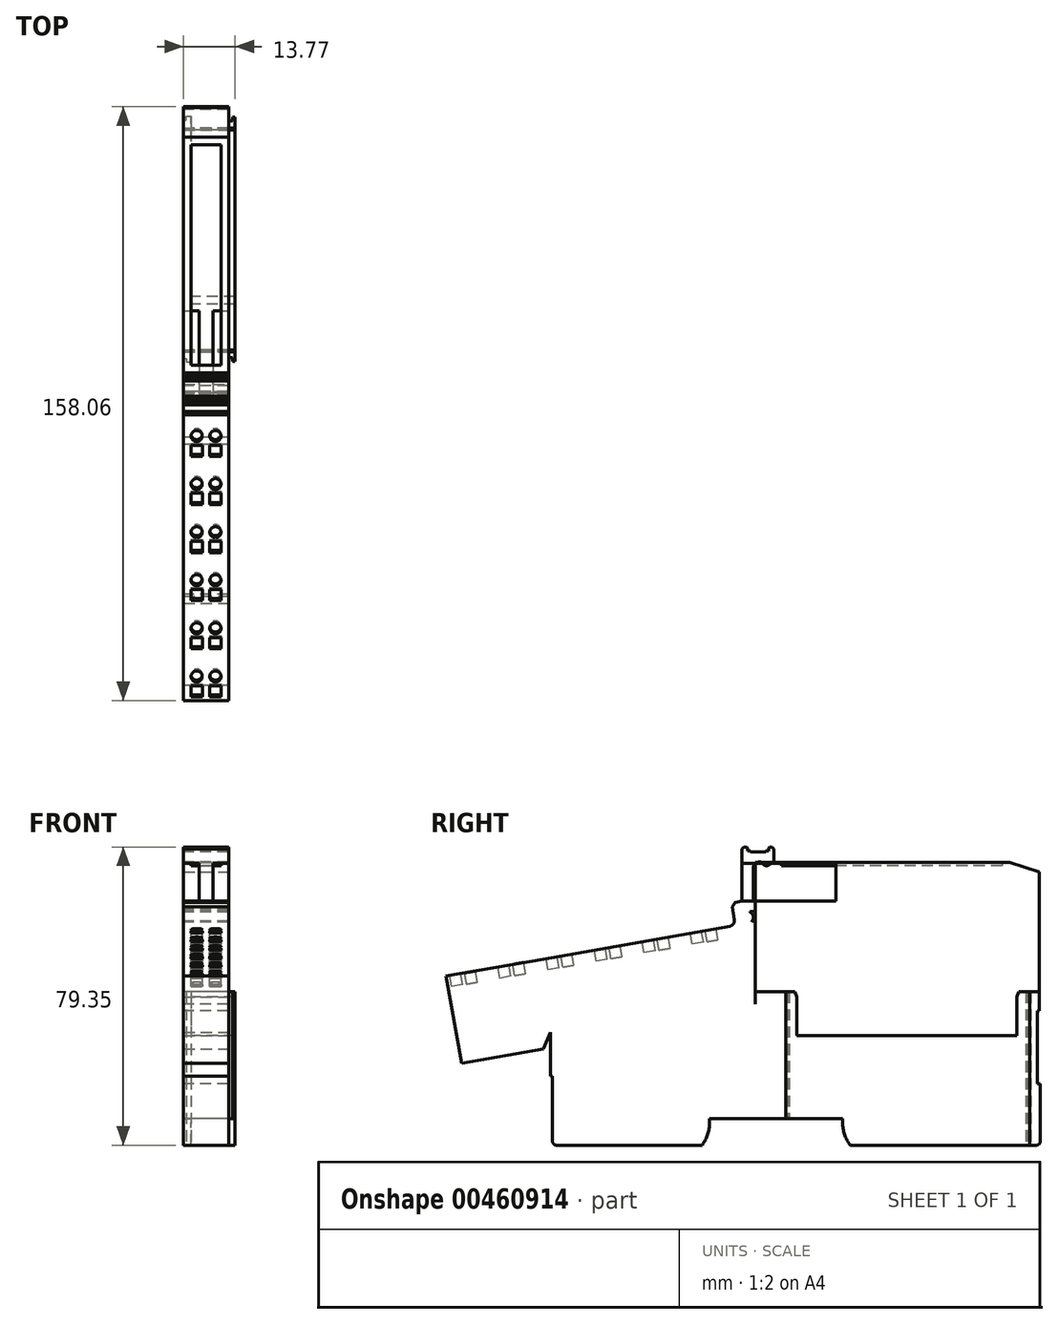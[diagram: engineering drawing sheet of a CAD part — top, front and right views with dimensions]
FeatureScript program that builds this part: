
annotation { "Feature Type Name" : "Feature", "Feature Type Description" : "" }
export const myFeature = defineFeature(function(context is Context, id is Id, definition is map)
    precondition{}
    {
        {
            var Q0;
            Q0=qCreatedBy(makeId("Right.planeOp"),FACE);
            var sketch = newSketch(context, id + "F0", { "sketchPlane" : qUnion([Q0])});
            skLineSegment(sketch, "E0", {"start": v(-59.26, 11.1) * mm, "end": v(-59.26, 24.1) * mm});
            skLineSegment(sketch, "E1", {"start": v(-58.76, -6.2) * mm, "end": v(-58.76, 11.1) * mm});
            skLineSegment(sketch, "E2", {"start": v(-57.26, 21.1) * mm, "end": v(-57.26, 21.9) * mm});
            skLineSegment(sketch, "E3", {"start": v(-57, 22.32) * mm, "end": v(-57, 22.69) * mm});
            skLineSegment(sketch, "E4", {"start": v(-62.03, 41.17) * mm, "end": v(-58.92, 23.54) * mm});
            skLineSegment(sketch, "E5", {"start": v(-8.32, 71.64) * mm, "end": v(-7.82, 72.14) * mm});
            skLineSegment(sketch, "E6", {"start": v(-57.76, -7.2) * mm, "end": v(-18.96, -7.2) * mm});
            skLineSegment(sketch, "E7", {"start": v(20.44, -7.2) * mm, "end": v(70, -7.2) * mm});
            skLineSegment(sketch, "E8", {"start": v(-1.27, 71.9) * mm, "end": v(-1.02, 72.14) * mm});
            skLineSegment(sketch, "E9", {"start": v(0.18, 68.14) * mm, "end": v(-1.32, 67.28) * mm});
            skLineSegment(sketch, "E10", {"start": v(-16.96, -0.2) * mm, "end": v(18.44, -0.2) * mm});
            skLineSegment(sketch, "E11", {"start": v(-10.97, 56.26) * mm, "end": v(-10.16, 57.42) * mm});
            skLineSegment(sketch, "E12", {"start": v(-16.96, -1.2) * mm, "end": v(-16.96, -0.2) * mm});
            skLineSegment(sketch, "E13", {"start": v(-4.8, 55.42) * mm, "end": v(-5.01, 55.13) * mm});
            skLineSegment(sketch, "E14", {"start": v(70.24, 9.16) * mm, "end": v(71, 9.16) * mm});
            skLineSegment(sketch, "E15", {"start": v(-59.26, 11.1) * mm, "end": v(-58.76, 11.1) * mm});
            skLineSegment(sketch, "E16", {"start": v(-8.32, 57.75) * mm, "end": v(-8.32, 71.64) * mm});
            skLineSegment(sketch, "E17", {"start": v(-6.87, 71.14) * mm, "end": v(-6.87, 71.9) * mm});
            skLineSegment(sketch, "E18", {"start": v(-5.32, 57.86) * mm, "end": v(-5.32, 66.64) * mm});
            skLineSegment(sketch, "E19", {"start": v(6.24, 21.9) * mm, "end": v(64.74, 21.9) * mm});
            skLineSegment(sketch, "E20", {"start": v(-10.97, 56.26) * mm, "end": v(-10.37, 52.82) * mm});
            skLineSegment(sketch, "E21", {"start": v(-4.8, 57.5) * mm, "end": v(-4.8, 55.42) * mm});
            skLineSegment(sketch, "E22", {"start": v(-4.8, 52.17) * mm, "end": v(-4.8, 30.34) * mm});
            skLineSegment(sketch, "E23", {"start": v(-4.76, 30.35) * mm, "end": v(-4.76, 33.6) * mm});
            skLineSegment(sketch, "E24", {"start": v(-1.27, 71.9) * mm, "end": v(-1.27, 71.14) * mm});
            skLineSegment(sketch, "E25", {"start": v(-59.26, 24.1) * mm, "end": v(-59.02, 24.1) * mm});
            skLineSegment(sketch, "E26", {"start": v(0.18, 68.14) * mm, "end": v(0.18, 71.64) * mm});
            skLineSegment(sketch, "E27", {"start": v(-57.26, 21.1) * mm, "end": v(-4.76, 30.35) * mm});
            skLineSegment(sketch, "E28", {"start": v(70.24, 28.6) * mm, "end": v(70.74, 28.6) * mm});
            skLineSegment(sketch, "E29", {"start": v(6.24, 21.9) * mm, "end": v(6.24, 32.22) * mm});
            skLineSegment(sketch, "E30", {"start": v(-58.92, 23.54) * mm, "end": v(-58.18, 23.67) * mm});
            skLineSegment(sketch, "E31", {"start": v(-4.76, 33.6) * mm, "end": v(5.74, 33.6) * mm});
            skLineSegment(sketch, "E32", {"start": v(65.24, 33.6) * mm, "end": v(70.74, 33.6) * mm});
            skLineSegment(sketch, "E33", {"start": v(5.74, 33.6) * mm, "end": v(6.24, 32.22) * mm});
            skLineSegment(sketch, "E34", {"start": v(-5.1, 52.38) * mm, "end": v(-4.8, 52.17) * mm});
            skLineSegment(sketch, "E35", {"start": v(18.44, -1.2) * mm, "end": v(18.44, -0.2) * mm});
            skLineSegment(sketch, "E36", {"start": v(-5.32, 57.86) * mm, "end": v(-4.8, 57.5) * mm});
            skLineSegment(sketch, "E37", {"start": v(-11.58, 51.08) * mm, "end": v(-61.22, 42.33) * mm});
            skLineSegment(sketch, "E38", {"start": v(-5.1, 52.38) * mm, "end": v(-5.74, 52.26) * mm});
            skLineSegment(sketch, "E39", {"start": v(-2.53, 67.44) * mm, "end": v(-3.24, 68.14) * mm});
            skLineSegment(sketch, "E40", {"start": v(-7.12, 72.14) * mm, "end": v(-6.87, 71.9) * mm});
            skLineSegment(sketch, "E41", {"start": v(-6.21, 54.92) * mm, "end": v(-5.01, 55.13) * mm});
            skLineSegment(sketch, "E42", {"start": v(-0.32, 72.14) * mm, "end": v(0.18, 71.64) * mm});
            skLineSegment(sketch, "E43", {"start": v(-8.32, 57.75) * mm, "end": v(-10.16, 57.42) * mm});
            skLineSegment(sketch, "E44", {"start": v(-3.82, 68.14) * mm, "end": v(-3.24, 68.14) * mm});
            skLineSegment(sketch, "E45", {"start": v(-6.07, 70.9) * mm, "end": v(-2.07, 70.9) * mm});
            skLineSegment(sketch, "E46", {"start": v(-1.27, 71.14) * mm, "end": v(-1.82, 71.14) * mm});
            skLineSegment(sketch, "E47", {"start": v(-6.32, 71.14) * mm, "end": v(-6.87, 71.14) * mm});
            skLineSegment(sketch, "E48", {"start": v(-0.32, 72.14) * mm, "end": v(-1.02, 72.14) * mm});
            skLineSegment(sketch, "E49", {"start": v(-7.12, 72.14) * mm, "end": v(-7.82, 72.14) * mm});
            skLineSegment(sketch, "E50", {"start": v(64.74, 32.22) * mm, "end": v(65.24, 33.6) * mm});
            skLineSegment(sketch, "E51", {"start": v(64.74, 21.9) * mm, "end": v(64.74, 32.22) * mm});
            skLineSegment(sketch, "E52", {"start": v(70.24, 9.16) * mm, "end": v(70.24, 28.6) * mm});
            skLineSegment(sketch, "E53", {"start": v(70.74, 28.6) * mm, "end": v(70.74, 33.6) * mm});
            skLineSegment(sketch, "E54", {"start": v(71, 9.16) * mm, "end": v(71, -6.2) * mm});
            skArc(sketch, "E55", {"start": v(-18.96, -7.2) * mm, "mid": v(-17.47, -4.37) * mm, "end": v(-16.96, -1.2) * mm});
            skArc(sketch, "E56", {"start": v(18.44, -1.2) * mm, "mid": v(18.95, -4.37) * mm, "end": v(20.44, -7.2) * mm});
            skArc(sketch, "E57", {"start": v(-6.21, 54.81) * mm, "mid": v(-5.35, 53.73) * mm, "end": v(-5.74, 52.4) * mm});
            skArc(sketch, "E58", {"start": v(-3.82, 68.14) * mm, "mid": v(-4.88, 67.7) * mm, "end": v(-5.32, 66.64) * mm});
            skArc(sketch, "E59", {"start": v(-11.58, 51.08) * mm, "mid": v(-10.62, 51.7) * mm, "end": v(-10.37, 52.82) * mm});
            skArc(sketch, "E60", {"start": v(-57.26, 21.9) * mm, "mid": v(-57.1, 22.1) * mm, "end": v(-57, 22.32) * mm});
            skArc(sketch, "E61", {"start": v(-2.53, 67.44) * mm, "mid": v(-1.95, 67.15) * mm, "end": v(-1.32, 67.28) * mm});
            skArc(sketch, "E62", {"start": v(-61.22, 42.33) * mm, "mid": v(-61.86, 41.92) * mm, "end": v(-62.03, 41.17) * mm});
            skArc(sketch, "E63", {"start": v(-57, 22.69) * mm, "mid": v(-57.37, 23.45) * mm, "end": v(-58.18, 23.67) * mm});
            skArc(sketch, "E64", {"start": v(-58.76, -6.2) * mm, "mid": v(-58.47, -6.91) * mm, "end": v(-57.76, -7.2) * mm});
            skArc(sketch, "E65", {"start": v(70, -7.2) * mm, "mid": v(70.7, -6.91) * mm, "end": v(71, -6.2) * mm});
            skArc(sketch, "E66", {"start": v(-6.07, 70.9) * mm, "mid": v(-6.15, 71.07) * mm, "end": v(-6.32, 71.14) * mm});
            skArc(sketch, "E67", {"start": v(-1.82, 71.14) * mm, "mid": v(-2, 71.07) * mm, "end": v(-2.07, 70.9) * mm});
            skLineSegment(sketch, "E68", {"start": v(-6.21, 54.92) * mm, "end": v(-6.21, 54.81) * mm});
            skLineSegment(sketch, "E69", {"start": v(-5.74, 52.26) * mm, "end": v(-5.74, 52.4) * mm});
            skSolve(sketch);
        }
        {
            var Q0;
            Q0=makeQuery(id+"F0.imprint","IMPRINT",FACE,{"disambiguationData":[TD([[makeQuery(id+"F0.imprint","IMPRINT",EDGE,{"derivedFrom":sQuery(id+"F0.wireOp",EDGE,"E0")}),-1.0]])]});
            extrude(context, id + "F1", {"entities" : qUnion([Q0]), "depth" : 25 * mm, "offsetDistance" : 25 * mm, "symmetric" : true});
        }
        {
            var Q0;
            {var subQ2=sQuery(id+"F0.wireOp",EDGE,"E2");Q0=makeQuery(id+"F0.imprint","IMPRINT",FACE,{"disambiguationData":[TD([[makeQuery(id+"F0.imprint","IMPRINT",EDGE,{"derivedFrom":subQ2}),-1.0]])]});}
            extrude(context, id + "F2", {"entities" : qUnion([Q0]), "depth" : 25 * mm, "offsetDistance" : 25 * mm, "symmetric" : true});
        }
        {
            var Q0;
            Q0=makeQuery(id+"F1.opExtrude","SWEPT_FACE",FACE,{"disambiguationData":[OSD([sQuery(id+"F0.wireOp",EDGE,"E7")])]});
            var sketch = newSketch(context, id + "F3", { "sketchPlane" : qUnion([Q0])});
            skLineSegment(sketch, "E70.MirrorCS", {"start": v(4.65, -4.25) * mm, "end": v(5.65, -4.25) * mm});
            skLineSegment(sketch, "E71.MirrorCS", {"start": v(5.65, -4.25) * mm, "end": v(5.65, -3.25) * mm});
            skLineSegment(sketch, "E72.MirrorCS", {"start": v(5.65, -3.25) * mm, "end": v(6.4, -3.25) * mm});
            skLineSegment(sketch, "E73.MirrorCS", {"start": v(-6.6, -67.5) * mm, "end": v(-6.6, -68.5) * mm});
            skLineSegment(sketch, "E74.MirrorCS", {"start": v(-6.6, -68.5) * mm, "end": v(-5.35, -68.5) * mm});
            skLineSegment(sketch, "E75.MirrorCS", {"start": v(-6.6, -4) * mm, "end": v(-7.35, -4) * mm});
            skLineSegment(sketch, "E76.MirrorCS", {"start": v(-7.37, -67.5) * mm, "end": v(-7.37, -72.33) * mm});
            skLineSegment(sketch, "E77.MirrorCS", {"start": v(-7.37, -67.5) * mm, "end": v(-6.6, -67.5) * mm});
            skLineSegment(sketch, "E78.MirrorCS", {"start": v(-6.6, -3) * mm, "end": v(-6.6, -4) * mm});
            skLineSegment(sketch, "E79.MirrorCS", {"start": v(-5.35, -3) * mm, "end": v(-6.6, -3) * mm});
            skLineSegment(sketch, "E80.MirrorCS", {"start": v(5.65, -67.25) * mm, "end": v(4.65, -67.25) * mm});
            skLineSegment(sketch, "E81.MirrorCS", {"start": v(4.65, -67.25) * mm, "end": v(4.65, -72.33) * mm});
            skLineSegment(sketch, "E82.MirrorCS", {"start": v(5.65, -68.25) * mm, "end": v(5.65, -67.25) * mm});
            skLineSegment(sketch, "E83.MirrorCS", {"start": v(6.4, -68.25) * mm, "end": v(5.65, -68.25) * mm});
            skLineSegment(sketch, "E84.MirrorCS", {"start": v(-5.35, -3) * mm, "end": v(-5.35, -68.5) * mm});
            skLineSegment(sketch, "E85.MirrorCS", {"start": v(6.4, -3.25) * mm, "end": v(6.4, -68.25) * mm});
            skLineSegment(sketch, "E86.MirrorCS", {"start": v(-7.35, -4) * mm, "end": v(-7.35, 62.03) * mm});
            skLineSegment(sketch, "E87.MirrorCS", {"start": v(4.65, 62.03) * mm, "end": v(-7.35, 62.03) * mm});
            skLineSegment(sketch, "E88.MirrorCS", {"start": v(-7.37, -72.33) * mm, "end": v(4.65, -72.33) * mm});
            skLineSegment(sketch, "E89.MirrorCS", {"start": v(4.65, 62.03) * mm, "end": v(4.65, -4.25) * mm});
            skLineSegment(sketch, "E90.bottom", {"start": v(43.3, -96.21) * mm, "end": v(-50.8, -96.21) * mm});
            skLineSegment(sketch, "E90.top", {"start": v(43.3, 101.45) * mm, "end": v(-50.8, 101.45) * mm});
            skLineSegment(sketch, "E90.left", {"start": v(43.3, -96.21) * mm, "end": v(43.3, 101.45) * mm});
            skLineSegment(sketch, "E90.right", {"start": v(-50.8, -96.21) * mm, "end": v(-50.8, 101.45) * mm});
            skSolve(sketch);
        }
        {
            var Q0;
            Q0=makeQuery(id+"F3.imprint","IMPRINT",FACE,{"disambiguationData":[TD([[makeQuery(id+"F3.imprint","IMPRINT",EDGE,{"derivedFrom":sQuery(id+"F3.wireOp",EDGE,"E70.MirrorCS")}),1.0]])]});
            var Q1;
            {var subQ2=sQuery(id+"F3.wireOp",EDGE,"E80.MirrorCS");Q1=makeQuery(id+"F3.imprint","IMPRINT",FACE,{"disambiguationData":[TD([[makeQuery(id+"F3.imprint","IMPRINT",EDGE,{"derivedFrom":subQ2}),1.0]])]});}
            var Q2;
            Q2=makeQuery(id+"F3.imprint","IMPRINT",FACE,{"disambiguationData":[TD([[makeQuery(id+"F3.imprint","IMPRINT",EDGE,{"derivedFrom":sQuery(id+"F3.wireOp",EDGE,"E73.MirrorCS")}),1.0]])]});
            extrude(context, id + "F4", {"entities" : qUnion([Q0, Q1, Q2]), "operationType" : NewBodyOperationType.REMOVE, "endBound" : BoundingType.THROUGH_ALL, "oppositeDirection" : true, "depth" : 25 * mm, "offsetDistance" : 25 * mm});
        }
        {
            var Q0;
            Q0=makeQuery(id+"F4.boolean.opBoolean","COPY",FACE,{"derivedFrom":makeQuery(id+"F4.opExtrude","SWEPT_FACE",FACE,{"disambiguationData":[OSD([sQuery(id+"F3.wireOp",EDGE,"E85.MirrorCS")])]})});
            var sketch = newSketch(context, id + "F5", { "sketchPlane" : qUnion([Q0])});
            skLineSegment(sketch, "E91.0", {"start": v(64.74, 21.9) * mm, "end": v(6.24, 21.9) * mm});
            skLineSegment(sketch, "E92.0", {"start": v(6.24, 32.22) * mm, "end": v(6.24, 21.9) * mm});
            skLineSegment(sketch, "E93.0", {"start": v(6.24, 32.22) * mm, "end": v(5.74, 33.6) * mm});
            skLineSegment(sketch, "E94.0", {"start": v(5.74, 33.6) * mm, "end": v(4.25, 33.6) * mm});
            skLineSegment(sketch, "E95.0", {"start": v(3.25, 33.6) * mm, "end": v(-4.76, 33.6) * mm});
            skPoint(sketch, "E96.orphan", {"position": v(3.25, 33.6) * mm});
            skLineSegment(sketch, "E97", {"start": v(3.25, 33.6) * mm, "end": v(4.25, 33.6) * mm});
            skLineSegment(sketch, "E98.0", {"start": v(64.74, 32.22) * mm, "end": v(64.74, 21.9) * mm});
            skLineSegment(sketch, "E98.1", {"start": v(65.24, 33.6) * mm, "end": v(64.74, 32.22) * mm});
            skLineSegment(sketch, "E98.2", {"start": v(67.25, 33.6) * mm, "end": v(65.24, 33.6) * mm});
            skLineSegment(sketch, "E98.3", {"start": v(70.74, 33.6) * mm, "end": v(68.25, 33.6) * mm});
            skPoint(sketch, "E99.orphan", {"position": v(67.25, 33.6) * mm});
            skLineSegment(sketch, "E100", {"start": v(67.25, 33.6) * mm, "end": v(68.25, 33.6) * mm});
            skLineSegment(sketch, "E101", {"start": v(-4.76, 33.6) * mm, "end": v(-4.76, 68.1) * mm});
            skLineSegment(sketch, "E102", {"start": v(-4.76, 68.1) * mm, "end": v(62.88, 68.1) * mm});
            skLineSegment(sketch, "E103", {"start": v(62.88, 68.1) * mm, "end": v(70.74, 65.5) * mm});
            skLineSegment(sketch, "E104", {"start": v(70.74, 65.5) * mm, "end": v(70.74, 33.6) * mm});
            skSolve(sketch);
        }
        {
            var Q0;
            Q0=makeQuery(id+"F5.imprint","IMPRINT",FACE,{"disambiguationData":[TD([[makeQuery(id+"F5.imprint","IMPRINT",EDGE,{"derivedFrom":sQuery(id+"F5.wireOp",EDGE,"E91.0")}),-1.0]])]});
            extrude(context, id + "F6", {"entities" : qUnion([Q0]), "oppositeDirection" : true, "depth" : 12 * mm, "offsetDistance" : 25 * mm});
        }
        {
            var Q0;
            Q0=makeQuery(id+"F6.opExtrude","SWEPT_BODY",BODY,{"disambiguationData":[OSD([sQuery(id+"F5.wireOp",EDGE,"E91.0"),sQuery(id+"F5.wireOp",EDGE,"E92.0"),sQuery(id+"F5.wireOp",EDGE,"E93.0"),sQuery(id+"F5.wireOp",EDGE,"E94.0"),sQuery(id+"F5.wireOp",EDGE,"E95.0"),sQuery(id+"F5.wireOp",EDGE,"E97"),sQuery(id+"F5.wireOp",EDGE,"E98.0"),sQuery(id+"F5.wireOp",EDGE,"E98.1"),sQuery(id+"F5.wireOp",EDGE,"E98.2"),sQuery(id+"F5.wireOp",EDGE,"E98.3"),sQuery(id+"F5.wireOp",EDGE,"E100"),sQuery(id+"F5.wireOp",EDGE,"E101"),sQuery(id+"F5.wireOp",EDGE,"E102"),sQuery(id+"F5.wireOp",EDGE,"E103"),sQuery(id+"F5.wireOp",EDGE,"E104")])]});
            var Q1;
            Q1=makeQuery(id+"F2.opExtrude","SWEPT_EDGE",EDGE,{"disambiguationData":[OSD([sQuery(id+"F0.wireOp",EDGE,"E16"),sQuery(id+"F0.wireOp",EDGE,"E43")])]});
            var Q2;
            Q2=makeQuery(id+"F2.opExtrude","SWEPT_EDGE",EDGE,{"disambiguationData":[OSD([sQuery(id+"F0.wireOp",EDGE,"E11"),sQuery(id+"F0.wireOp",EDGE,"E20")])]});
            transform(context, id + "F7", {"entities" : qUnion([Q0]), "transformType" : TransformType.TRANSLATION_DISTANCE, "transformDirection" : qUnion([Q2]), "distance" : 1.75 * mm, "makeCopy" : false});
        }
        {
            var Q0;
            Q0=makeQuery(id+"F2.opExtrude","SWEPT_FACE",FACE,{"disambiguationData":[OSD([sQuery(id+"F0.wireOp",EDGE,"E16")])]});
            var sketch = newSketch(context, id + "F8", { "sketchPlane" : qUnion([Q0])});
            skLineSegment(sketch, "E105.bottom", {"start": v(-7.35, 67.79) * mm, "end": v(-3.24, 67.79) * mm});
            skLineSegment(sketch, "E105.top", {"start": v(-7.35, 57.75) * mm, "end": v(-3.24, 57.75) * mm});
            skLineSegment(sketch, "E105.left", {"start": v(-7.35, 67.79) * mm, "end": v(-7.35, 57.75) * mm});
            skLineSegment(sketch, "E105.right", {"start": v(-3.24, 67.79) * mm, "end": v(-3.24, 57.75) * mm});
            skLineSegment(sketch, "E106.bottom", {"start": v(0.54, 67.79) * mm, "end": v(4.65, 67.79) * mm});
            skLineSegment(sketch, "E106.top", {"start": v(0.54, 57.75) * mm, "end": v(4.65, 57.75) * mm});
            skLineSegment(sketch, "E106.left", {"start": v(0.54, 67.79) * mm, "end": v(0.54, 57.75) * mm});
            skLineSegment(sketch, "E106.right", {"start": v(4.65, 67.79) * mm, "end": v(4.65, 57.75) * mm});
            skSolve(sketch);
        }
        {
            var Q0;
            Q0=makeQuery(id+"F8.imprint","IMPRINT",FACE,{"disambiguationData":[TD([[makeQuery(id+"F8.imprint","IMPRINT",EDGE,{"derivedFrom":sQuery(id+"F8.wireOp",EDGE,"E105.bottom")}),-1.0]])]});
            var Q1;
            Q1=makeQuery(id+"F8.imprint","IMPRINT",FACE,{"disambiguationData":[TD([[makeQuery(id+"F8.imprint","IMPRINT",EDGE,{"derivedFrom":sQuery(id+"F8.wireOp",EDGE,"E106.bottom")}),-1.0]])]});
            extrude(context, id + "F9", {"entities" : qUnion([Q0, Q1]), "operationType" : NewBodyOperationType.REMOVE, "oppositeDirection" : true, "depth" : 25 * mm, "offsetDistance" : 25 * mm});
        }
        {
            var Q0;
            Q0=makeQuery(id+"F6.opExtrude","SWEPT_FACE",FACE,{"disambiguationData":[OSD([sQuery(id+"F5.wireOp",EDGE,"E102")])]});
            var sketch = newSketch(context, id + "F10", { "sketchPlane" : qUnion([Q0])});
            skLineSegment(sketch, "E107.bottom", {"start": v(-5.35, 60.88) * mm, "end": v(2.65, 60.88) * mm});
            skLineSegment(sketch, "E107.top", {"start": v(-5.35, 2.18) * mm, "end": v(2.65, 2.18) * mm});
            skLineSegment(sketch, "E107.left", {"start": v(-5.35, 60.88) * mm, "end": v(-5.35, 2.18) * mm});
            skLineSegment(sketch, "E107.right", {"start": v(2.65, 60.88) * mm, "end": v(2.65, 2.18) * mm});
            skSolve(sketch);
        }
        {
            var Q0;
            Q0=makeQuery(id+"F10.imprint","IMPRINT",FACE,{"disambiguationData":[TD([[makeQuery(id+"F10.imprint","IMPRINT",EDGE,{"derivedFrom":sQuery(id+"F10.wireOp",EDGE,"E107.bottom")}),-1.0]])]});
            extrude(context, id + "F11", {"entities" : qUnion([Q0]), "operationType" : NewBodyOperationType.REMOVE, "oppositeDirection" : true, "depth" : 1 * mm, "offsetDistance" : 25 * mm});
        }
        {
            var Q0;
            Q0=makeQuery(id+"F11.boolean.opBoolean","COPY",FACE,{"derivedFrom":makeQuery(id+"F11.opExtrude","CAP_FACE",FACE,{"disambiguationData":[OSD([sQuery(id+"F10.wireOp",EDGE,"E107.bottom"),sQuery(id+"F10.wireOp",EDGE,"E107.top"),sQuery(id+"F10.wireOp",EDGE,"E107.left"),sQuery(id+"F10.wireOp",EDGE,"E107.right")])],"isStart":false})});
            extrude(context, id + "F12", {"entities" : qUnion([Q0]), "depth" : 1 * mm, "offsetDistance" : 25 * mm});
        }
        {
            var Q0;
            {var subQ18=makeQuery(id+"F2.opExtrude","SWEPT_FACE",FACE,{"disambiguationData":[OSD([sQuery(id+"F0.wireOp",EDGE,"E2")])]});Q0=makeQuery(id+"F9.boolean.opBoolean","SPLIT",FACE,{"disambiguationData":[TD([subQ18])],"derivedFrom":makeQuery(id+"F4.boolean.opBoolean","COPY",FACE,{"disambiguationData":[TD([subQ18])],"derivedFrom":makeQuery(id+"F4.opExtrude","SWEPT_FACE",FACE,{"disambiguationData":[OSD([sQuery(id+"F3.wireOp",EDGE,"E89.MirrorCS")])]})})});}
            var sketch = newSketch(context, id + "F13", { "sketchPlane" : qUnion([Q0])});
            skLineSegment(sketch, "E108", {"start": v(-61.22, 42.33) * mm, "end": v(-87.07, 37.77) * mm});
            skLineSegment(sketch, "E109", {"start": v(-87.07, 37.77) * mm, "end": v(-82.97, 14.53) * mm});
            skLineSegment(sketch, "E110", {"start": v(-82.97, 14.53) * mm, "end": v(-61.22, 18.36) * mm});
            skLineSegment(sketch, "E111", {"start": v(-61.22, 18.36) * mm, "end": v(-58.92, 23.54) * mm});
            skSolve(sketch);
        }
        {
            var Q0;
            Q0=makeQuery(id+"F13.imprint","IMPRINT",FACE,{"disambiguationData":[TD([[makeQuery(id+"F13.imprint","IMPRINT",EDGE,{"derivedFrom":sQuery(id+"F13.wireOp",EDGE,"E108")}),1.0]])]});
            var Q1;
            {var subQ18=makeQuery(id+"F2.opExtrude","SWEPT_FACE",FACE,{"disambiguationData":[OSD([sQuery(id+"F0.wireOp",EDGE,"E2")])]});Q1=makeQuery(id+"F9.boolean.opBoolean","SPLIT",FACE,{"disambiguationData":[TD([subQ18])],"derivedFrom":makeQuery(id+"F4.boolean.opBoolean","COPY",FACE,{"disambiguationData":[TD([subQ18])],"derivedFrom":makeQuery(id+"F4.opExtrude","SWEPT_FACE",FACE,{"disambiguationData":[OSD([sQuery(id+"F3.wireOp",EDGE,"E86.MirrorCS")])]})})});}
            extrude(context, id + "F14", {"entities" : qUnion([Q0]), "operationType" : NewBodyOperationType.ADD, "endBound" : BoundingType.UP_TO_SURFACE, "oppositeDirection" : true, "depth" : 25 * mm, "endBoundEntityFace" : qUnion([Q1]), "offsetDistance" : 25 * mm});
        }
        {
            var Q0;
            Q0=makeQuery(id+"F2.opExtrude","SWEPT_FACE",FACE,{"disambiguationData":[OSD([sQuery(id+"F0.wireOp",EDGE,"E37")])]});
            var sketch = newSketch(context, id + "F15", { "sketchPlane" : qUnion([Q0])});
            skLineSegment(sketch, "E112", {"start": v(-1.35, -52.94) * mm, "end": v(-1.35, -2.54) * mm, "construction": true});
            skLineSegment(sketch, "E113.bottom", {"start": v(-5.35, -75.19) * mm, "end": v(-2.35, -75.19) * mm});
            skLineSegment(sketch, "E113.top", {"start": v(-5.35, -78.19) * mm, "end": v(-2.35, -78.19) * mm});
            skLineSegment(sketch, "E113.left", {"start": v(-5.35, -75.19) * mm, "end": v(-5.35, -78.19) * mm});
            skLineSegment(sketch, "E113.right", {"start": v(-2.35, -75.19) * mm, "end": v(-2.35, -78.19) * mm});
            skCircle(sketch, "E114", {"center": v(-3.85, -72.69) * mm, "radius": 1.5 * mm});
            skPoint(sketch, "E114.centerSnap0", {"position": v(-3.85, -75.19) * mm});
            skCircle(sketch, "E115.0.1.0", {"center": v(-3.85, -59.69) * mm, "radius": 1.5 * mm});
            skLineSegment(sketch, "E115.0.1.1", {"start": v(-5.35, -62.19) * mm, "end": v(-2.35, -62.19) * mm});
            skLineSegment(sketch, "E115.0.1.2", {"start": v(-2.35, -62.19) * mm, "end": v(-2.35, -65.19) * mm});
            skLineSegment(sketch, "E115.0.1.3", {"start": v(-5.35, -65.19) * mm, "end": v(-2.35, -65.19) * mm});
            skLineSegment(sketch, "E115.0.1.4", {"start": v(-5.35, -62.19) * mm, "end": v(-5.35, -65.19) * mm});
            skCircle(sketch, "E115.0.2.0", {"center": v(-3.85, -46.69) * mm, "radius": 1.5 * mm});
            skLineSegment(sketch, "E115.0.2.1", {"start": v(-5.35, -49.19) * mm, "end": v(-2.35, -49.19) * mm});
            skLineSegment(sketch, "E115.0.2.2", {"start": v(-2.35, -49.19) * mm, "end": v(-2.35, -52.19) * mm});
            skLineSegment(sketch, "E115.0.2.3", {"start": v(-5.35, -52.19) * mm, "end": v(-2.35, -52.19) * mm});
            skLineSegment(sketch, "E115.0.2.4", {"start": v(-5.35, -49.19) * mm, "end": v(-5.35, -52.19) * mm});
            skCircle(sketch, "E115.0.3.0", {"center": v(-3.85, -33.69) * mm, "radius": 1.5 * mm});
            skLineSegment(sketch, "E115.0.3.1", {"start": v(-5.35, -36.19) * mm, "end": v(-2.35, -36.19) * mm});
            skLineSegment(sketch, "E115.0.3.2", {"start": v(-2.35, -36.19) * mm, "end": v(-2.35, -39.19) * mm});
            skLineSegment(sketch, "E115.0.3.3", {"start": v(-5.35, -39.19) * mm, "end": v(-2.35, -39.19) * mm});
            skLineSegment(sketch, "E115.0.3.4", {"start": v(-5.35, -36.19) * mm, "end": v(-5.35, -39.19) * mm});
            skCircle(sketch, "E115.1.0.0", {"center": v(1.15, -72.69) * mm, "radius": 1.5 * mm});
            skLineSegment(sketch, "E115.1.0.1", {"start": v(-0.35, -75.19) * mm, "end": v(2.65, -75.19) * mm});
            skLineSegment(sketch, "E115.1.0.2", {"start": v(2.65, -75.19) * mm, "end": v(2.65, -78.19) * mm});
            skLineSegment(sketch, "E115.1.0.3", {"start": v(-0.35, -78.19) * mm, "end": v(2.65, -78.19) * mm});
            skLineSegment(sketch, "E115.1.0.4", {"start": v(-0.35, -75.19) * mm, "end": v(-0.35, -78.19) * mm});
            skCircle(sketch, "E115.1.1.0", {"center": v(1.15, -59.69) * mm, "radius": 1.5 * mm});
            skLineSegment(sketch, "E115.1.1.1", {"start": v(-0.35, -62.19) * mm, "end": v(2.65, -62.19) * mm});
            skLineSegment(sketch, "E115.1.1.2", {"start": v(2.65, -62.19) * mm, "end": v(2.65, -65.19) * mm});
            skLineSegment(sketch, "E115.1.1.3", {"start": v(-0.35, -65.19) * mm, "end": v(2.65, -65.19) * mm});
            skLineSegment(sketch, "E115.1.1.4", {"start": v(-0.35, -62.19) * mm, "end": v(-0.35, -65.19) * mm});
            skCircle(sketch, "E115.1.2.0", {"center": v(1.15, -46.69) * mm, "radius": 1.5 * mm});
            skLineSegment(sketch, "E115.1.2.1", {"start": v(-0.35, -49.19) * mm, "end": v(2.65, -49.19) * mm});
            skLineSegment(sketch, "E115.1.2.2", {"start": v(2.65, -49.19) * mm, "end": v(2.65, -52.19) * mm});
            skLineSegment(sketch, "E115.1.2.3", {"start": v(-0.35, -52.19) * mm, "end": v(2.65, -52.19) * mm});
            skLineSegment(sketch, "E115.1.2.4", {"start": v(-0.35, -49.19) * mm, "end": v(-0.35, -52.19) * mm});
            skCircle(sketch, "E115.1.3.0", {"center": v(1.15, -33.69) * mm, "radius": 1.5 * mm});
            skLineSegment(sketch, "E115.1.3.1", {"start": v(-0.35, -36.19) * mm, "end": v(2.65, -36.19) * mm});
            skLineSegment(sketch, "E115.1.3.2", {"start": v(2.65, -36.19) * mm, "end": v(2.65, -39.19) * mm});
            skLineSegment(sketch, "E115.1.3.3", {"start": v(-0.35, -39.19) * mm, "end": v(2.65, -39.19) * mm});
            skLineSegment(sketch, "E115.1.3.4", {"start": v(-0.35, -36.19) * mm, "end": v(-0.35, -39.19) * mm});
            skLineSegment(sketch, "E115.direction1", {"start": v(-3.85, -72.69) * mm, "end": v(1.15, -72.69) * mm, "construction": true});
            skLineSegment(sketch, "E115.direction2", {"start": v(-3.85, -72.69) * mm, "end": v(-3.85, -59.69) * mm, "construction": true});
            skCircle(sketch, "E116.0.0.4", {"center": v(-3.85, -20.69) * mm, "radius": 1.5 * mm});
            skLineSegment(sketch, "E116.2.0.4", {"start": v(-5.35, -23.19) * mm, "end": v(-2.35, -23.19) * mm});
            skLineSegment(sketch, "E116.5.0.4", {"start": v(-2.35, -23.19) * mm, "end": v(-2.35, -26.19) * mm});
            skLineSegment(sketch, "E116.8.0.4", {"start": v(-5.35, -26.19) * mm, "end": v(-2.35, -26.19) * mm});
            skLineSegment(sketch, "E116.11.0.4", {"start": v(-5.35, -23.19) * mm, "end": v(-5.35, -26.19) * mm});
            skCircle(sketch, "E116.0.0.5", {"center": v(-3.85, -7.69) * mm, "radius": 1.5 * mm});
            skLineSegment(sketch, "E116.2.0.5", {"start": v(-5.35, -10.19) * mm, "end": v(-2.35, -10.19) * mm});
            skLineSegment(sketch, "E116.5.0.5", {"start": v(-2.35, -10.19) * mm, "end": v(-2.35, -13.19) * mm});
            skLineSegment(sketch, "E116.8.0.5", {"start": v(-5.35, -13.19) * mm, "end": v(-2.35, -13.19) * mm});
            skLineSegment(sketch, "E116.11.0.5", {"start": v(-5.35, -10.19) * mm, "end": v(-5.35, -13.19) * mm});
            skCircle(sketch, "E116.0.1.4", {"center": v(1.15, -20.69) * mm, "radius": 1.5 * mm});
            skLineSegment(sketch, "E116.2.1.4", {"start": v(-0.35, -23.19) * mm, "end": v(2.65, -23.19) * mm});
            skLineSegment(sketch, "E116.5.1.4", {"start": v(2.65, -23.19) * mm, "end": v(2.65, -26.19) * mm});
            skLineSegment(sketch, "E116.8.1.4", {"start": v(-0.35, -26.19) * mm, "end": v(2.65, -26.19) * mm});
            skLineSegment(sketch, "E116.11.1.4", {"start": v(-0.35, -23.19) * mm, "end": v(-0.35, -26.19) * mm});
            skCircle(sketch, "E116.0.1.5", {"center": v(1.15, -7.69) * mm, "radius": 1.5 * mm});
            skLineSegment(sketch, "E116.2.1.5", {"start": v(-0.35, -10.19) * mm, "end": v(2.65, -10.19) * mm});
            skLineSegment(sketch, "E116.5.1.5", {"start": v(2.65, -10.19) * mm, "end": v(2.65, -13.19) * mm});
            skLineSegment(sketch, "E116.8.1.5", {"start": v(-0.35, -13.19) * mm, "end": v(2.65, -13.19) * mm});
            skLineSegment(sketch, "E116.11.1.5", {"start": v(-0.35, -10.19) * mm, "end": v(-0.35, -13.19) * mm});
            skSolve(sketch);
        }
        {
            var Q0;
            Q0 = qSketchRegion(id + "F15", true);
            extrude(context, id + "F16", {"entities" : qUnion([Q0]), "operationType" : NewBodyOperationType.REMOVE, "oppositeDirection" : true, "depth" : 3 * mm, "offsetDistance" : 25 * mm});
        }
    });
